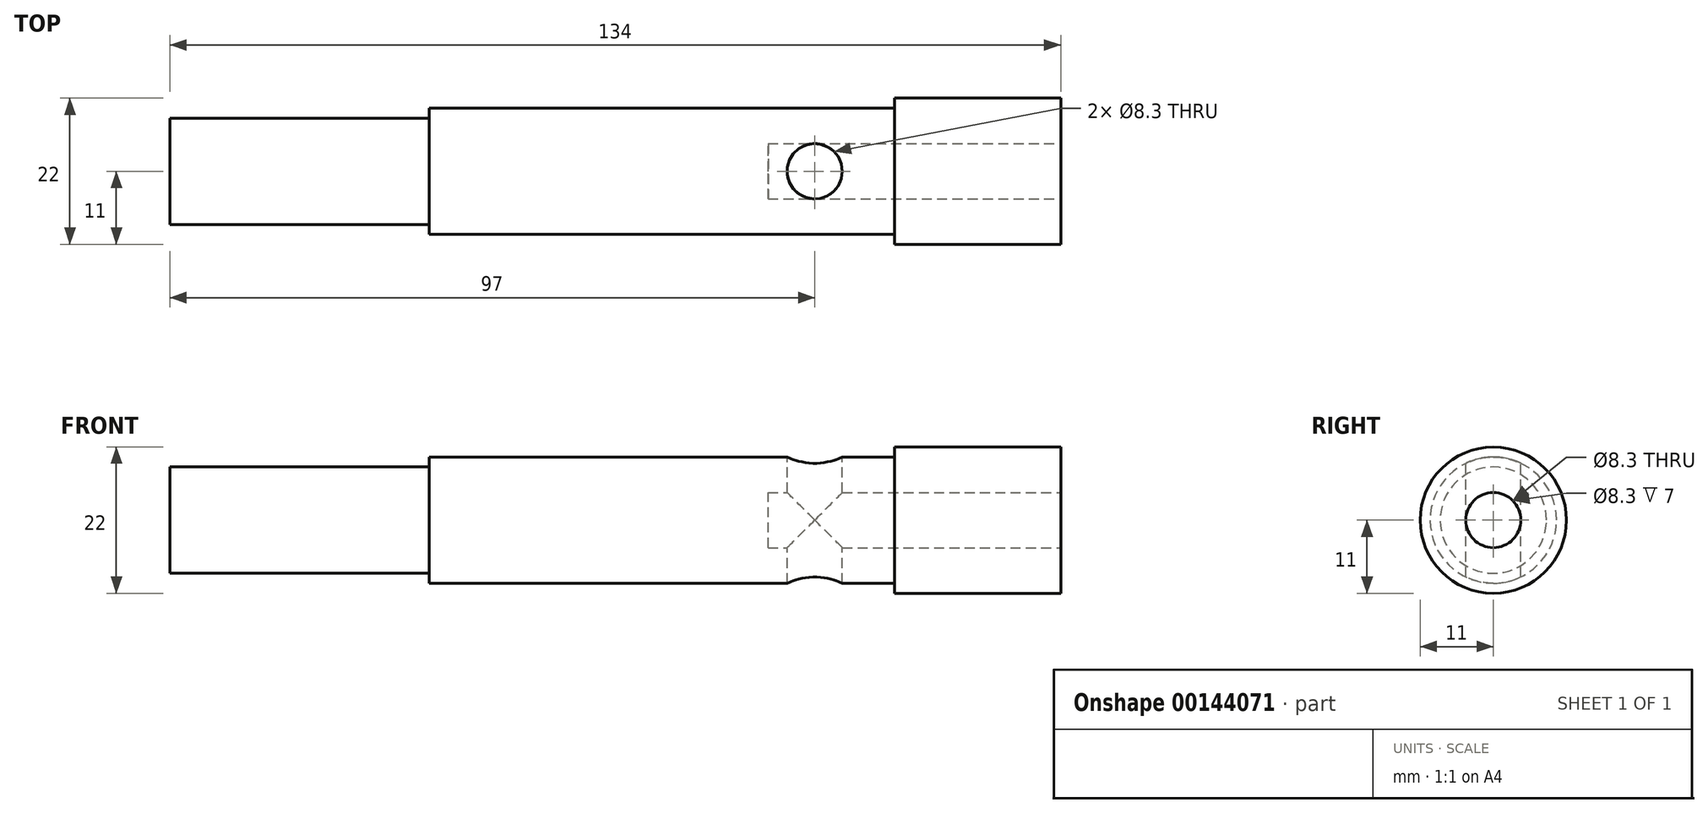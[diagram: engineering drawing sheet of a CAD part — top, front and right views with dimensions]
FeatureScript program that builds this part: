
annotation { "Feature Type Name" : "Feature", "Feature Type Description" : "" }
export const myFeature = defineFeature(function(context is Context, id is Id, definition is map)
    precondition{}
    {
        {
            var Q0;
            Q0=qCreatedBy(makeId("Right.planeOp"),FACE);
            var sketch = newSketch(context, id + "F0", { "sketchPlane" : qUnion([Q0])});
            skCircle(sketch, "E0", {"center": v(0, 0) * mm, "radius": 11 * mm});
            skSolve(sketch);
        }
        {
            var Q0;
            Q0=makeQuery(id+"F0.imprint","IMPRINT",FACE,{"disambiguationData":[TD([[makeQuery(id+"F0.imprint","IMPRINT",EDGE,{"derivedFrom":sQuery(id+"F0.wireOp",EDGE,"E0")}),1.0]])]});
            extrude(context, id + "F1", {"entities" : qUnion([Q0]), "endBound" : BoundingType.SYMMETRIC, "depth" : 134 * mm});
        }
        {
            var Q0;
            Q0=makeQuery(id+"F1.opExtrude","CAP_FACE",FACE,{"disambiguationData":[OSD([sQuery(id+"F0.wireOp",EDGE,"E0")])],"isStart":false});
            cPlane(context, id + "F2", {"entities" : qUnion([Q0]), "cplaneType" : CPlaneType.OFFSET, "offset" : 25 * mm, "oppositeDirection" : true, "width" : 150 * mm, "height" : 150 * mm});
        }
        {
            var Q0;
            Q0=qCreatedBy(id+"F2.planeOp",FACE);
            var sketch = newSketch(context, id + "F3", { "sketchPlane" : qUnion([Q0])});
            skCircle(sketch, "E1", {"center": v(0, 0) * mm, "radius": 9.5 * mm});
            skCircle(sketch, "E2", {"center": v(0, 0) * mm, "radius": 11 * mm});
            skSolve(sketch);
        }
        {
            var Q0;
            Q0=makeQuery(id+"F3.imprint","IMPRINT",FACE,{"disambiguationData":[TD([[makeQuery(id+"F3.imprint","IMPRINT",EDGE,{"derivedFrom":sQuery(id+"F3.wireOp",EDGE,"E1")}),-1.0]])]});
            extrude(context, id + "F4", {"entities" : qUnion([Q0]), "operationType" : NewBodyOperationType.REMOVE, "oppositeDirection" : true, "depth" : 70 * mm});
        }
        {
            var Q0;
            Q0=makeQuery(id+"F4.boolean.opBoolean","COPY",FACE,{"derivedFrom":makeQuery(id+"F4.opExtrude","CAP_FACE",FACE,{"disambiguationData":[OSD([sQuery(id+"F3.wireOp",EDGE,"E1"),sQuery(id+"F3.wireOp",EDGE,"E2")])],"isStart":false})});
            cPlane(context, id + "F5", {"entities" : qUnion([Q0]), "cplaneType" : CPlaneType.OFFSET, "offset" : 0 * mm, "width" : 150 * mm, "height" : 150 * mm});
        }
        {
            var Q0;
            Q0=qCreatedBy(id+"F5.planeOp",FACE);
            var sketch = newSketch(context, id + "F6", { "sketchPlane" : qUnion([Q0])});
            skCircle(sketch, "E3", {"center": v(0, 0) * mm, "radius": 8 * mm});
            skCircle(sketch, "E4", {"center": v(0, 0) * mm, "radius": 11 * mm});
            skSolve(sketch);
        }
        {
            var Q0;
            Q0=makeQuery(id+"F6.imprint","IMPRINT",FACE,{"disambiguationData":[TD([[makeQuery(id+"F6.imprint","IMPRINT",EDGE,{"derivedFrom":sQuery(id+"F6.wireOp",EDGE,"E3")}),-1.0]])]});
            extrude(context, id + "F7", {"entities" : qUnion([Q0]), "operationType" : NewBodyOperationType.REMOVE, "endBound" : BoundingType.THROUGH_ALL, "oppositeDirection" : true, "depth" : 25 * mm});
        }
        {
            var Q0;
            Q0=makeQuery(id+"F1.opExtrude","CAP_FACE",FACE,{"disambiguationData":[OSD([sQuery(id+"F0.wireOp",EDGE,"E0")])],"isStart":false});
            var sketch = newSketch(context, id + "F8", { "sketchPlane" : qUnion([Q0])});
            skCircle(sketch, "E5", {"center": v(0, 0) * mm, "radius": 4.15 * mm});
            skSolve(sketch);
        }
        {
            var Q0;
            Q0=makeQuery(id+"F8.imprint","IMPRINT",FACE,{"disambiguationData":[TD([[makeQuery(id+"F8.imprint","IMPRINT",EDGE,{"derivedFrom":sQuery(id+"F8.wireOp",EDGE,"E5")}),1.0]])]});
            extrude(context, id + "F9", {"entities" : qUnion([Q0]), "operationType" : NewBodyOperationType.REMOVE, "oppositeDirection" : true, "depth" : 44 * mm});
        }
        {
            var Q0;
            Q0=qCreatedBy(makeId("Top.planeOp"),FACE);
            cPlane(context, id + "F10", {"entities" : qUnion([Q0]), "cplaneType" : CPlaneType.OFFSET, "offset" : 9.5 * mm, "width" : 150 * mm, "height" : 150 * mm});
        }
        {
            var Q0;
            Q0=qCreatedBy(id+"F10.planeOp",FACE);
            var sketch = newSketch(context, id + "F11", { "sketchPlane" : qUnion([Q0])});
            skCircle(sketch, "E6", {"center": v(30, 0) * mm, "radius": 4.15 * mm});
            skSolve(sketch);
        }
        {
            var Q0;
            Q0=makeQuery(id+"F11.imprint","IMPRINT",FACE,{"disambiguationData":[TD([[makeQuery(id+"F11.imprint","IMPRINT",EDGE,{"derivedFrom":sQuery(id+"F11.wireOp",EDGE,"E6")}),1.0]])]});
            extrude(context, id + "F12", {"entities" : qUnion([Q0]), "operationType" : NewBodyOperationType.REMOVE, "endBound" : BoundingType.THROUGH_ALL, "oppositeDirection" : true, "depth" : 25 * mm});
        }
    });
